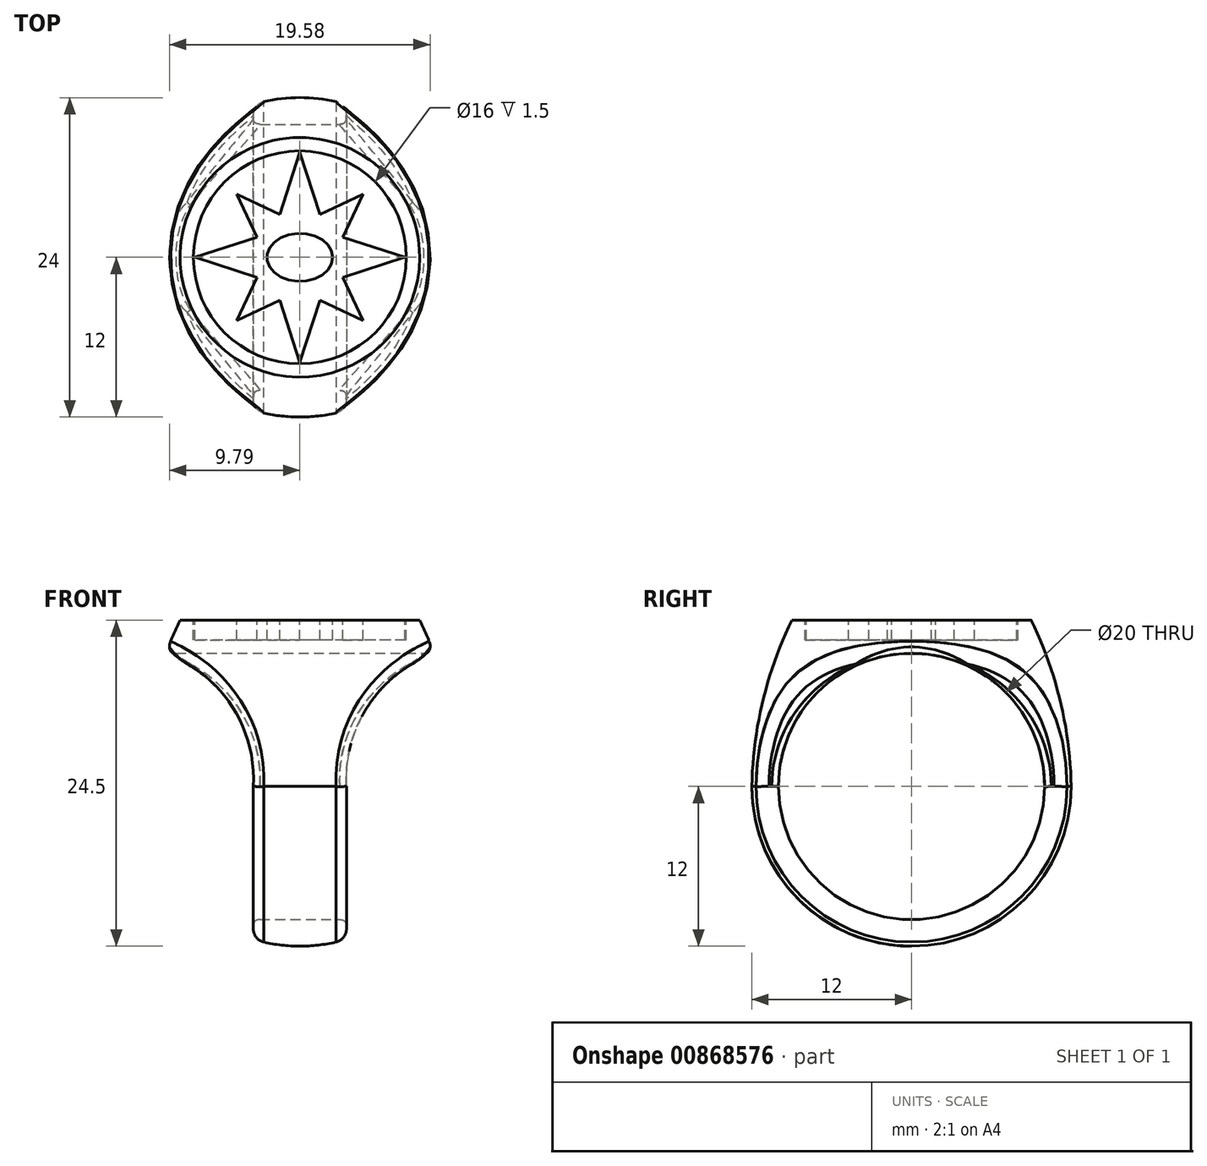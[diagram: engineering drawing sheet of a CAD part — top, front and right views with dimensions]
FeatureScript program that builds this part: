
annotation { "Feature Type Name" : "Feature", "Feature Type Description" : "" }
export const myFeature = defineFeature(function(context is Context, id is Id, definition is map)
    precondition{}
    {
        {
            var Q0;
            Q0=qCreatedBy(makeId("Right.planeOp"),FACE);
            var sketch = newSketch(context, id + "F0", { "sketchPlane" : qUnion([Q0])});
            skLineSegment(sketch, "E0", {"start": v(0, 0) * mm, "end": v(0, -24.5) * mm});
            skLineSegment(sketch, "E1", {"start": v(0, 0) * mm, "end": v(-9, 0) * mm});
            skArc(sketch, "E2", {"start": v(-12, -12.5) * mm, "mid": v(-8.49, -20.99) * mm, "end": v(0, -24.5) * mm});
            skLineSegment(sketch, "E3", {"start": v(0, -12.5) * mm, "end": v(-12, -12.5) * mm, "construction": true});
            skArc(sketch, "E4", {"start": v(-9, 0) * mm, "mid": v(-11.18, -6.09) * mm, "end": v(-12, -12.5) * mm});
            skSolve(sketch);
        }
        {
            var Q0;
            Q0=makeQuery(id+"F0.imprint","IMPRINT",FACE,{"disambiguationData":[TD([[makeQuery(id+"F0.imprint","IMPRINT",EDGE,{"derivedFrom":sQuery(id+"F0.wireOp",EDGE,"E0")}),-1.0]])]});
            var Q1;
            Q1=sQuery(id+"F0.wireOp",EDGE,"E0");
            revolve(context, id + "F1", {"entities" : qUnion([Q0]), "axis" : qUnion([Q1]), "revolveType" : RevolveType.FULL});
        }
        {
            var Q0;
            Q0=qCreatedBy(makeId("Right.planeOp"),FACE);
            var sketch = newSketch(context, id + "F2", { "sketchPlane" : qUnion([Q0])});
            skCircle(sketch, "E5", {"center": v(0, -12.5) * mm, "radius": 10 * mm});
            skSolve(sketch);
        }
        {
            var Q0;
            Q0=qSketchRegion(id+"F2",true);
            extrude(context, id + "F3", {"entities" : qUnion([Q0]), "operationType" : NewBodyOperationType.REMOVE, "endBound" : BoundingType.SYMMETRIC, "oppositeDirection" : true, "depth" : 25 * mm, "offsetDistance" : 25 * mm});
        }
        {
            var Q0;
            Q0=qCreatedBy(makeId("Front.planeOp"),FACE);
            var sketch = newSketch(context, id + "F4", { "sketchPlane" : qUnion([Q0])});
            skLineSegment(sketch, "E6", {"start": v(3.5, -26.5) * mm, "end": v(3.5, -12.5) * mm});
            skArc(sketch, "E7", {"start": v(10.15, -2.5) * mm, "mid": v(5.16, -6.39) * mm, "end": v(3.5, -12.5) * mm});
            skLineSegment(sketch, "E8", {"start": v(10.15, -2.5) * mm, "end": v(11.65, -2.5) * mm});
            skLineSegment(sketch, "E9", {"start": v(11.65, -2.5) * mm, "end": v(11.65, -26.5) * mm});
            skLineSegment(sketch, "E10", {"start": v(11.65, -26.5) * mm, "end": v(3.5, -26.5) * mm});
            skPoint(sketch, "E11.start.orphan", {"position": v(0, -24.5) * mm});
            skLineSegment(sketch, "E12", {"start": v(0, 0) * mm, "end": v(0, -24.5) * mm, "construction": true});
            skLineSegment(sketch, "E13.MirrorCS", {"start": v(-3.5, -26.5) * mm, "end": v(-3.5, -12.5) * mm});
            skArc(sketch, "E14.MirrorCS", {"start": v(-10.15, -2.5) * mm, "mid": v(-5.16, -6.39) * mm, "end": v(-3.5, -12.5) * mm});
            skLineSegment(sketch, "E15.MirrorCS", {"start": v(-11.65, -2.5) * mm, "end": v(-11.65, -26.5) * mm});
            skLineSegment(sketch, "E16.MirrorCS", {"start": v(-11.65, -26.5) * mm, "end": v(-3.5, -26.5) * mm});
            skLineSegment(sketch, "E17.MirrorCS", {"start": v(-10.15, -2.5) * mm, "end": v(-11.65, -2.5) * mm});
            skSolve(sketch);
        }
        {
            var Q0;
            Q0=qSketchRegion(id+"F4",true);
            extrude(context, id + "F5", {"entities" : qUnion([Q0]), "operationType" : NewBodyOperationType.REMOVE, "endBound" : BoundingType.SYMMETRIC, "depth" : 25 * mm, "offsetDistance" : 25 * mm});
        }
        {
            var Q0;
            Q0=makeQuery(id+"F1.opRevolve","SWEPT_FACE",FACE,{"disambiguationData":[OSD([sQuery(id+"F0.wireOp",EDGE,"E1")])]});
            var sketch = newSketch(context, id + "F6", { "sketchPlane" : qUnion([Q0])});
            skCircle(sketch, "E18", {"center": v(0, 0) * mm, "radius": 8 * mm});
            skLineSegment(sketch, "E19", {"start": v(-8, 0) * mm, "end": v(8, 0) * mm, "construction": true});
            skEllipse(sketch, "E20", {"center": v(0, 0) * mm, "majorRadius": 2.47 * mm, "minorRadius": 1.8 * mm, "majorAxis": v(1, 0)});
            skLineSegment(sketch, "E21", {"start": v(0, 8) * mm, "end": v(0, -8) * mm, "construction": true});
            skPoint(sketch, "E21.startSnap0", {"position": v(0, 1.8) * mm});
            skPoint(sketch, "E21.endSnap0", {"position": v(0, -1.8) * mm});
            skLineSegment(sketch, "E22", {"start": v(0, 0) * mm, "end": v(5.66, -5.66) * mm, "construction": true});
            skCircle(sketch, "E23", {"center": v(0, 0) * mm, "radius": 3.55 * mm, "construction": true});
            skLineSegment(sketch, "E24", {"start": v(7.9, 0) * mm, "end": v(3.22, -1.5) * mm});
            skLineSegment(sketch, "E25", {"start": v(3.22, -1.5) * mm, "end": v(4.74, -4.74) * mm});
            skLineSegment(sketch, "E26", {"start": v(4.74, -4.74) * mm, "end": v(1.5, -3.22) * mm});
            skLineSegment(sketch, "E27", {"start": v(1.5, -3.22) * mm, "end": v(0, -7.9) * mm});
            skLineSegment(sketch, "E28.MirrorCS", {"start": v(1.5, 3.22) * mm, "end": v(0, 7.9) * mm});
            skLineSegment(sketch, "E29.MirrorCS", {"start": v(4.74, 4.74) * mm, "end": v(1.5, 3.22) * mm});
            skLineSegment(sketch, "E30.MirrorCS", {"start": v(3.22, 1.5) * mm, "end": v(4.74, 4.74) * mm});
            skLineSegment(sketch, "E31.MirrorCS", {"start": v(7.9, 0) * mm, "end": v(3.22, 1.5) * mm});
            skLineSegment(sketch, "E32.MirrorCS", {"start": v(-1.5, 3.22) * mm, "end": v(0, 7.9) * mm});
            skLineSegment(sketch, "E33.MirrorCS", {"start": v(-4.74, 4.74) * mm, "end": v(-1.5, 3.22) * mm});
            skLineSegment(sketch, "E34.MirrorCS", {"start": v(-3.22, 1.5) * mm, "end": v(-4.74, 4.74) * mm});
            skLineSegment(sketch, "E35.MirrorCS", {"start": v(-7.9, 0) * mm, "end": v(-3.22, 1.5) * mm});
            skLineSegment(sketch, "E36.MirrorCS", {"start": v(-7.9, 0) * mm, "end": v(-3.22, -1.5) * mm});
            skLineSegment(sketch, "E37.MirrorCS", {"start": v(-4.74, -4.74) * mm, "end": v(-1.5, -3.22) * mm});
            skLineSegment(sketch, "E38.MirrorCS", {"start": v(-1.5, -3.22) * mm, "end": v(0, -7.9) * mm});
            skLineSegment(sketch, "E39.MirrorCS", {"start": v(-3.22, -1.5) * mm, "end": v(-4.74, -4.74) * mm});
            skSolve(sketch);
        }
        {
            var Q0;
            Q0=makeQuery(id+"F6.imprint","IMPRINT",FACE,{"disambiguationData":[TD([[makeQuery(id+"F6.imprint","IMPRINT",EDGE,{"derivedFrom":sQuery(id+"F6.wireOp",EDGE,"E18")}),1.0]])]});
            var Q1;
            Q1=makeQuery(id+"F6.imprint","IMPRINT",FACE,{"disambiguationData":[TD([[makeQuery(id+"F6.imprint","IMPRINT",EDGE,{"derivedFrom":sQuery(id+"F6.wireOp",EDGE,"E20")}),1.0]])]});
            extrude(context, id + "F7", {"entities" : qUnion([Q0, Q1]), "operationType" : NewBodyOperationType.REMOVE, "oppositeDirection" : true, "depth" : 1.5 * mm, "offsetDistance" : 25 * mm});
        }
        {
            var Q0;
            Q0=makeQuery(id+"F5.boolean.opBoolean","INTERSECT",EDGE,{"disambiguationData":[OD(1.0)],"derivedFrom":[makeQuery(id+"F1.opRevolve","SWEPT_FACE",FACE,{"disambiguationData":[OSD([sQuery(id+"F0.wireOp",EDGE,"E4")])]}),makeQuery(id+"F5.opExtrude","SWEPT_FACE",FACE,{"disambiguationData":[OSD([sQuery(id+"F4.wireOp",EDGE,"E14.MirrorCS")])]})]});
            var Q1;
            Q1=makeQuery(id+"F5.boolean.opBoolean","INTERSECT",EDGE,{"derivedFrom":[makeQuery(id+"F1.opRevolve","SWEPT_FACE",FACE,{"disambiguationData":[OSD([sQuery(id+"F0.wireOp",EDGE,"E2")])]}),makeQuery(id+"F5.opExtrude","SWEPT_FACE",FACE,{"disambiguationData":[OSD([sQuery(id+"F4.wireOp",EDGE,"E13.MirrorCS")])]})]});
            var Q2;
            Q2=makeQuery(id+"F5.boolean.opBoolean","INTERSECT",EDGE,{"disambiguationData":[OD(1.0)],"derivedFrom":[makeQuery(id+"F1.opRevolve","SWEPT_FACE",FACE,{"disambiguationData":[OSD([sQuery(id+"F0.wireOp",EDGE,"E4")])]}),makeQuery(id+"F5.opExtrude","SWEPT_FACE",FACE,{"disambiguationData":[OSD([sQuery(id+"F4.wireOp",EDGE,"E7")])]})]});
            var Q3;
            Q3=makeQuery(id+"F5.boolean.opBoolean","INTERSECT",EDGE,{"derivedFrom":[makeQuery(id+"F1.opRevolve","SWEPT_FACE",FACE,{"disambiguationData":[OSD([sQuery(id+"F0.wireOp",EDGE,"E2")])]}),makeQuery(id+"F5.opExtrude","SWEPT_FACE",FACE,{"disambiguationData":[OSD([sQuery(id+"F4.wireOp",EDGE,"E6")])]})]});
            fillet(context, id + "F8", {"entities" : qUnion([Q0, Q1, Q2, Q3]), "radius" : 1 * mm, "allowEdgeOverflow" : false});
        }
        {
            var Q0;
            Q0=makeQuery(id+"F5.boolean.opBoolean","INTERSECT",EDGE,{"disambiguationData":[OD(1.0)],"derivedFrom":[makeQuery(id+"F3.boolean.opBoolean","COPY",FACE,{"derivedFrom":makeQuery(id+"F3.opExtrude","SWEPT_FACE",FACE,{"disambiguationData":[OSD([sQuery(id+"F2.wireOp",EDGE,"E5")])]})}),makeQuery(id+"F5.opExtrude","SWEPT_FACE",FACE,{"disambiguationData":[OSD([sQuery(id+"F4.wireOp",EDGE,"E14.MirrorCS")])]})]});
            var Q1;
            Q1=makeQuery(id+"F5.boolean.opBoolean","INTERSECT",EDGE,{"derivedFrom":[makeQuery(id+"F3.boolean.opBoolean","COPY",FACE,{"derivedFrom":makeQuery(id+"F3.opExtrude","SWEPT_FACE",FACE,{"disambiguationData":[OSD([sQuery(id+"F2.wireOp",EDGE,"E5")])]})}),makeQuery(id+"F5.opExtrude","SWEPT_FACE",FACE,{"disambiguationData":[OSD([sQuery(id+"F4.wireOp",EDGE,"E13.MirrorCS")])]})]});
            var Q2;
            Q2=makeQuery(id+"F5.boolean.opBoolean","INTERSECT",EDGE,{"disambiguationData":[OD(0.0)],"derivedFrom":[makeQuery(id+"F3.boolean.opBoolean","COPY",FACE,{"derivedFrom":makeQuery(id+"F3.opExtrude","SWEPT_FACE",FACE,{"disambiguationData":[OSD([sQuery(id+"F2.wireOp",EDGE,"E5")])]})}),makeQuery(id+"F5.opExtrude","SWEPT_FACE",FACE,{"disambiguationData":[OSD([sQuery(id+"F4.wireOp",EDGE,"E14.MirrorCS")])]})]});
            var Q3;
            Q3=makeQuery(id+"F5.boolean.opBoolean","INTERSECT",EDGE,{"disambiguationData":[OD(0.0)],"derivedFrom":[makeQuery(id+"F3.boolean.opBoolean","COPY",FACE,{"derivedFrom":makeQuery(id+"F3.opExtrude","SWEPT_FACE",FACE,{"disambiguationData":[OSD([sQuery(id+"F2.wireOp",EDGE,"E5")])]})}),makeQuery(id+"F5.opExtrude","SWEPT_FACE",FACE,{"disambiguationData":[OSD([sQuery(id+"F4.wireOp",EDGE,"E7")])]})]});
            var Q4;
            Q4=makeQuery(id+"F3.boolean.opBoolean","COPY",FACE,{"derivedFrom":makeQuery(id+"F3.opExtrude","SWEPT_FACE",FACE,{"disambiguationData":[OSD([sQuery(id+"F2.wireOp",EDGE,"E5")])]})});
            fillet(context, id + "F9", {"entities" : qUnion([Q0, Q1, Q2, Q3, Q4]), "radius" : .5 * mm, "rho" : 0.5, "crossSection" : FilletCrossSection.CONIC, "allowEdgeOverflow" : false});
        }
    });
